# Revit family: FallProtection_Skylight_Kattsafe_Raised
name_source: partatom
category: Specialty Equipment
units: mm (PartAtom-declared; Revit-internal decimal feet)

## family parameters
Always vertical = No
Cut with Voids When Loaded = No
Enable Cutting in Views = No
Maintain Annotation Orientation = No
OmniClass Number = 23.27.71.21
Part Type = Normal
Room Calculation Point = No
Round Connector Dimension = Use Diameter
Shared = No
Work Plane-Based = Yes

## types (2) — shared parameters
Assembly Code = E1090100
Default Elevation = 1219 mm
Description = Skylight protectors provide fall hazard protection for brittle skylights and roof surfaces without compromising light penetration. Available in multiple configurations and sizes, Kattsafe skylight protectors work well with all types of roof lights, skylights and brittle roof structures.
ElementType = Fall Protection
Export Type to IFC As = IfcBuildingElementProxy
FrameMaterial = Aluminum_Kattsafe_Satin
IfcExportAs = IfcBuildingElementProxy
IfcExportType = USERDEFINED
Manufacturer = Kattsafe®
ManufacturerOverallHeight = 300 mm
ManufacturerURLProductSpecific = https://kattsafe.com.au
Material = Aluminum_Kattsafe_Mesh_Protex
ModifiedIssue = 20240430 $
Type IFC Predefined Type = USERDEFINED
URL = https://kattsafe.com.au
Uniclass2015Code = Pr_30_59_84
Uniclass2015Title = Shutters and grilles
Uniclass2015Version = Products v1.23

## per-type parameters (varying)
| type | ManufacturerOverallLength | ManufacturerOverallWidth | ManufacturerSpecCode | Model | Type Comments |
| 800l x 835w x 300h (SP395.800) | 800 mm  [stored 2.62467 ft] | 835 mm | SP395.800 | SP395.800 | Raised Skylight Protector - 800(L) x 835(W) x 300(H) |
| 1200l x 1250w x 300h (SP395.1200) | 1200 mm  [stored 3.93701 ft] | 1250 mm  [stored 4.10105 ft] | SP395.1200 | SP395.1200 | Raised Skylight Protector - 1200(L) x 1250(W) x 300(H) |

note: [stored X ft] marks values corroborated as IEEE doubles in the binary element streams (Revit-internal decimal feet)

## geometry (parser evidence)
native form markers: Sweep x3
no freeform markers — native parametric forms only
